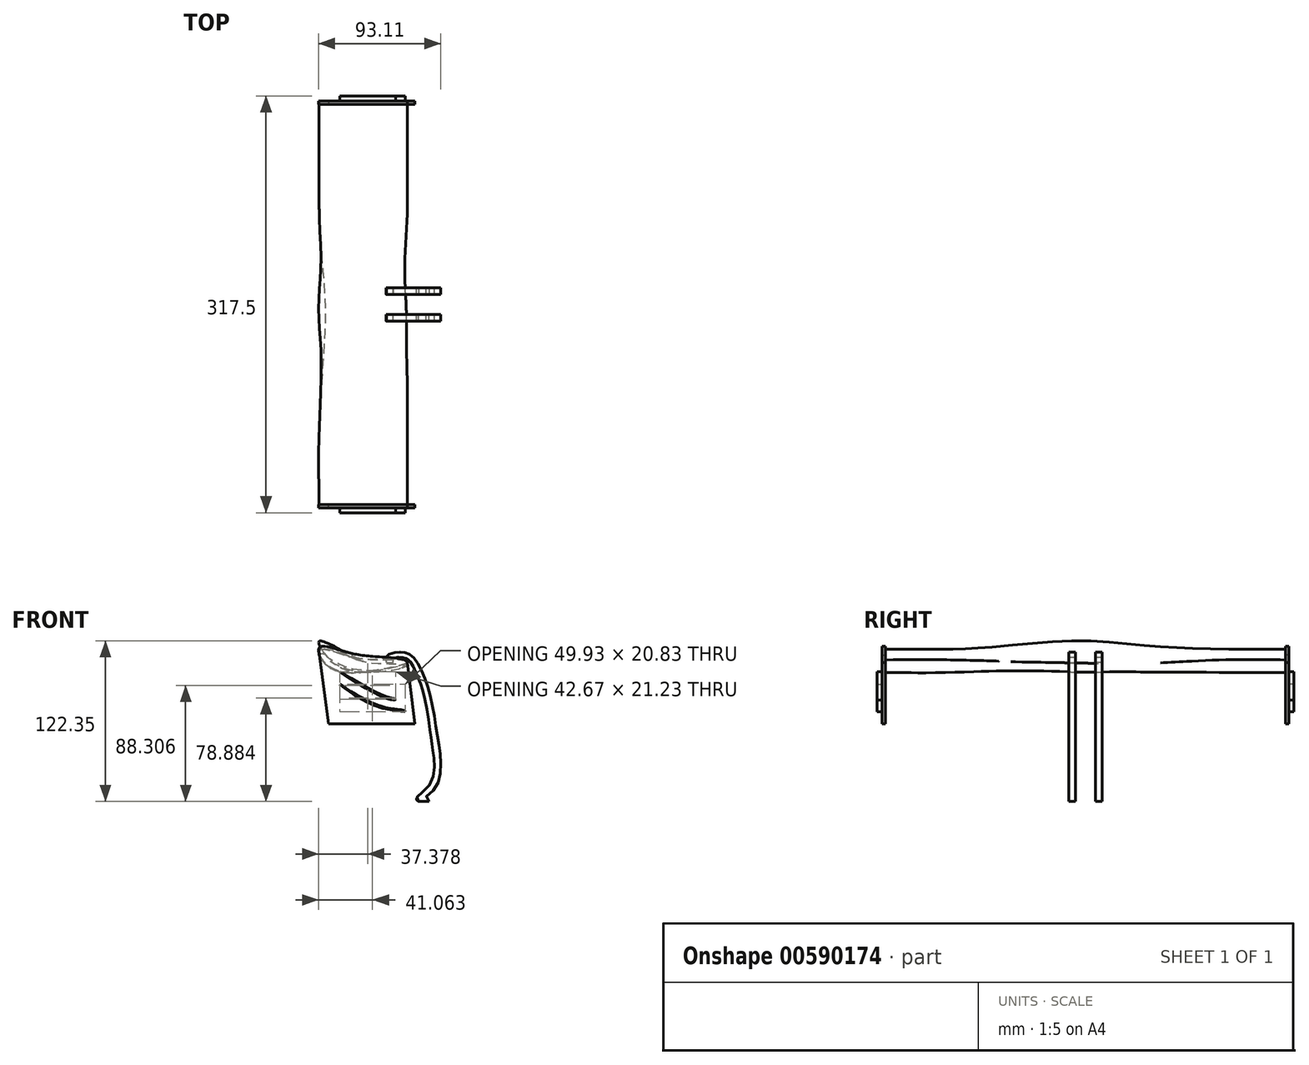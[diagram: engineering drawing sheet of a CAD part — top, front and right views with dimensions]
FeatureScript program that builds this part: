
annotation { "Feature Type Name" : "Feature", "Feature Type Description" : "" }
export const myFeature = defineFeature(function(context is Context, id is Id, definition is map)
    precondition{}
    {
        {
            var Q0;
            Q0=qCreatedBy(makeId("Front.planeOp"),FACE);
            cPlane(context, id + "F0", {"entities" : qUnion([Q0]), "cplaneType" : CPlaneType.OFFSET, "offset" : 50.8 * mm, "width" : 152.4 * mm, "height" : 152.4 * mm});
        }
        {
            var Q0;
            Q0=qCreatedBy(makeId("Front.planeOp"),FACE);
            cPlane(context, id + "F1", {"entities" : qUnion([Q0]), "cplaneType" : CPlaneType.OFFSET, "offset" : 101.6 * mm, "width" : 152.4 * mm, "height" : 152.4 * mm});
        }
        {
            var Q0;
            Q0=qCreatedBy(makeId("Front.planeOp"),FACE);
            cPlane(context, id + "F2", {"entities" : qUnion([Q0]), "cplaneType" : CPlaneType.OFFSET, "offset" : 152.4 * mm, "width" : 152.4 * mm, "height" : 152.4 * mm});
        }
        {
            var Q0;
            Q0=qCreatedBy(makeId("Front.planeOp"),FACE);
            cPlane(context, id + "F3", {"entities" : qUnion([Q0]), "cplaneType" : CPlaneType.OFFSET, "offset" : 203.2 * mm, "width" : 152.4 * mm, "height" : 152.4 * mm});
        }
        {
            var Q0;
            Q0=qCreatedBy(makeId("Front.planeOp"),FACE);
            var sketch = newSketch(context, id + "F4", { "sketchPlane" : qUnion([Q0])});
            skFitSpline(sketch, "E0", {"points": [v(-32.08, 8.38) * mm, v(-24.09, -3.15) * mm, v(7.76, -6.56) * mm, v(34.95, -0.3) * mm, v(34.95, 0.54) * mm, v(23.88, 1.97) * mm, v(-3.04, 3.1) * mm, v(-26.45, 10.12) * mm, v(-32.08, 8.38) * mm]});
            skSolve(sketch);
        }
        {
            var Q0;
            Q0=qCreatedBy(id+"F3.planeOp",FACE);
            var sketch = newSketch(context, id + "F5", { "sketchPlane" : qUnion([Q0])});
            skFitSpline(sketch, "E1", {"points": [v(-32.08, 8.38) * mm, v(-24.09, -3.15) * mm, v(7.76, -6.56) * mm, v(34.95, -0.3) * mm, v(34.95, 0.54) * mm, v(23.88, 1.97) * mm, v(-3.04, 3.1) * mm, v(-26.45, 10.12) * mm, v(-32.08, 8.38) * mm]});
            skSolve(sketch);
        }
        {
            var Q0;
            Q0=qCreatedBy(id+"F2.planeOp",FACE);
            var sketch = newSketch(context, id + "F6", { "sketchPlane" : qUnion([Q0])});
            skFitSpline(sketch, "E2", {"points": [v(-30.58, 9.5) * mm, v(-19.7, 0) * mm, v(6.57, -6.28) * mm, v(34.6, -1.74) * mm, v(34.6, -0.9) * mm, v(23.53, 0.54) * mm, v(-3.98, 3.65) * mm, v(-26.15, 13.6) * mm, v(-30.58, 9.5) * mm]});
            skSolve(sketch);
        }
        {
            var Q0;
            Q0=qCreatedBy(id+"F3.planeOp",FACE);
            cPlane(context, id + "F7", {"entities" : qUnion([Q0]), "cplaneType" : CPlaneType.OFFSET, "offset" : 50.8 * mm, "width" : 152.4 * mm, "height" : 152.4 * mm});
        }
        {
            var Q0;
            Q0=qCreatedBy(makeId("Front.planeOp"),FACE);
            cPlane(context, id + "F8", {"entities" : qUnion([Q0]), "cplaneType" : CPlaneType.OFFSET, "offset" : 50.8 * mm, "oppositeDirection" : true, "width" : 152.4 * mm, "height" : 152.4 * mm});
        }
        {
            var Q0;
            Q0=qCreatedBy(id+"F1.planeOp",FACE);
            var sketch = newSketch(context, id + "F9", { "sketchPlane" : qUnion([Q0])});
            skFitSpline(sketch, "E3", {"points": [v(-32.4, 15.38) * mm, v(-20.36, -1.02) * mm, v(5.9, -7.3) * mm, v(33.93, -2.76) * mm, v(33.93, -1.92) * mm, v(22.86, -0.49) * mm, v(-4.64, 2.63) * mm, v(-30.73, 16.4) * mm, v(-32.4, 15.38) * mm]});
            skSolve(sketch);
        }
        {
            var Q0;
            Q0=qCreatedBy(id+"F0.planeOp",FACE);
            var sketch = newSketch(context, id + "F10", { "sketchPlane" : qUnion([Q0])});
            skFitSpline(sketch, "E4", {"points": [v(-31.25, 8.48) * mm, v(-20.36, -1.02) * mm, v(5.9, -7.3) * mm, v(33.93, -2.76) * mm, v(33.93, -1.92) * mm, v(22.86, -0.49) * mm, v(-4.64, 2.63) * mm, v(-26.82, 12.57) * mm, v(-31.25, 8.48) * mm]});
            skSolve(sketch);
        }
        {
            var Q0;
            Q0=qCreatedBy(id+"F7.planeOp",FACE);
            var sketch = newSketch(context, id + "F11", { "sketchPlane" : qUnion([Q0])});
            skFitSpline(sketch, "E5", {"points": [v(-32.08, 8.38) * mm, v(-24.09, -3.15) * mm, v(7.76, -6.56) * mm, v(34.95, -0.3) * mm, v(34.95, 0.54) * mm, v(23.88, 1.97) * mm, v(-3.04, 3.1) * mm, v(-26.45, 10.12) * mm, v(-32.08, 8.38) * mm]});
            skSolve(sketch);
        }
        {
            var Q0;
            Q0=qCreatedBy(id+"F8.planeOp",FACE);
            var sketch = newSketch(context, id + "F12", { "sketchPlane" : qUnion([Q0])});
            skFitSpline(sketch, "E6", {"points": [v(-32.08, 8.38) * mm, v(-24.09, -3.15) * mm, v(7.76, -6.56) * mm, v(34.95, -0.3) * mm, v(34.95, 0.54) * mm, v(23.88, 1.97) * mm, v(-3.04, 3.1) * mm, v(-26.45, 10.12) * mm, v(-32.08, 8.38) * mm]});
            skSolve(sketch);
        }
        {
            var Q0;
            Q0=makeQuery(id+"F11.imprint","IMPRINT",FACE,{"disambiguationData":[TD([[makeQuery(id+"F11.imprint","IMPRINT",EDGE,{"derivedFrom":sQuery(id+"F11.wireOp",EDGE,"E5")}),1.0]])]});
            var Q1;
            Q1=makeQuery(id+"F5.imprint","IMPRINT",FACE,{"disambiguationData":[TD([[makeQuery(id+"F5.imprint","IMPRINT",EDGE,{"derivedFrom":sQuery(id+"F5.wireOp",EDGE,"E1")}),1.0]])]});
            var Q2;
            Q2=makeQuery(id+"F6.imprint","IMPRINT",FACE,{"disambiguationData":[TD([[makeQuery(id+"F6.imprint","IMPRINT",EDGE,{"derivedFrom":sQuery(id+"F6.wireOp",EDGE,"E2")}),1.0]])]});
            var Q3;
            Q3=makeQuery(id+"F9.imprint","IMPRINT",FACE,{"disambiguationData":[TD([[makeQuery(id+"F9.imprint","IMPRINT",EDGE,{"derivedFrom":sQuery(id+"F9.wireOp",EDGE,"E3")}),1.0]])]});
            var Q4;
            Q4=makeQuery(id+"F10.imprint","IMPRINT",FACE,{"disambiguationData":[TD([[makeQuery(id+"F10.imprint","IMPRINT",EDGE,{"derivedFrom":sQuery(id+"F10.wireOp",EDGE,"E4")}),1.0]])]});
            var Q5;
            Q5=makeQuery(id+"F4.imprint","IMPRINT",FACE,{"disambiguationData":[TD([[makeQuery(id+"F4.imprint","IMPRINT",EDGE,{"derivedFrom":sQuery(id+"F4.wireOp",EDGE,"E0")}),1.0]])]});
            var Q6;
            Q6=makeQuery(id+"F12.imprint","IMPRINT",FACE,{"disambiguationData":[TD([[makeQuery(id+"F12.imprint","IMPRINT",EDGE,{"derivedFrom":sQuery(id+"F12.wireOp",EDGE,"E6")}),1.0]])]});
            loft(context, id + "F13", {"sheetProfilesArray" : [{ "sheetProfileEntities" : qUnion([Q0]) }, { "sheetProfileEntities" : qUnion([Q1]) }, { "sheetProfileEntities" : qUnion([Q2]) }, { "sheetProfileEntities" : qUnion([Q3]) }, { "sheetProfileEntities" : qUnion([Q4]) }, { "sheetProfileEntities" : qUnion([Q5]) }, { "sheetProfileEntities" : qUnion([Q6]) }]});
        }
        {
            var Q0;
            Q0=qCreatedBy(id+"F8.planeOp",FACE);
            var sketch = newSketch(context, id + "F14", { "sketchPlane" : qUnion([Q0])});
            skLineSegment(sketch, "E7", {"start": v(40.97, -46.8) * mm, "end": v(-24.74, -46.8) * mm});
            skFitSpline(sketch, "E8", {"points": [v(35.16, 0) * mm, v(1.01, 5.43) * mm, v(-26.43, 12.16) * mm, v(-31.74, 5.63) * mm], "startDerivative": vector(5.48, 30.94) * mm, "endDerivative": vector(34.9, -100.77) * mm});
            skLineSegment(sketch, "E9", {"start": v(35.16, 0) * mm, "end": v(40.97, -46.8) * mm});
            skLineSegment(sketch, "E10", {"start": v(20.11, -39.48) * mm, "end": v(16.28, -8.63) * mm});
            skLineSegment(sketch, "E11", {"start": v(16.28, -8.63) * mm, "end": v(14.52, -8.63) * mm});
            skLineSegment(sketch, "E12", {"start": v(20.11, -39.48) * mm, "end": v(18.36, -39.48) * mm});
            skLineSegment(sketch, "E13", {"start": v(18.36, -39.48) * mm, "end": v(14.52, -8.63) * mm});
            skLineSegment(sketch, "E14", {"start": v(-31.74, 5.63) * mm, "end": v(-24.74, -46.8) * mm});
            skSolve(sketch);
        }
        {
            var Q0;
            Q0=sQuery(id+"F14.wireOp",EDGE,"E7");
            var Q1;
            Q1=sQuery(id+"F14.wireOp",EDGE,"E8");
            loft(context, id + "F15", {"bodyType" : ToolBodyType.SURFACE, "wireProfilesArray" : [{ "wireProfileEntities" : qUnion([Q0]) }, { "wireProfileEntities" : qUnion([Q1]) }]});
        }
        {
            var Q0;
            Q0=makeQuery(id+"F15.opLoft","SWEPT_FACE",FACE,{"disambiguationData":[OSD([sQuery(id+"F14.wireOp",VERTEX,"E7.start"),sQuery(id+"F14.wireOp",VERTEX,"E7.end"),sQuery(id+"F14.wireOp",VERTEX,"E8.start"),sQuery(id+"F14.wireOp",VERTEX,"E8.end"),sQuery(id+"F14.wireOp",EDGE,"E7"),sQuery(id+"F14.wireOp",EDGE,"E8")])]});
            extrude(context, id + "F16", {"entities" : qUnion([Q0]), "operationType" : NewBodyOperationType.ADD, "depth" : 2.54 * mm, "offsetDistance" : 25.4 * mm});
        }
        {
            var Q0;
            Q0=makeQuery(id+"F16.opExtrude","CAP_FACE",FACE,{"disambiguationData":[OSD([sQuery(id+"F14.wireOp",VERTEX,"E7.start"),sQuery(id+"F14.wireOp",VERTEX,"E7.end"),sQuery(id+"F14.wireOp",VERTEX,"E8.start"),sQuery(id+"F14.wireOp",VERTEX,"E8.end"),sQuery(id+"F14.wireOp",EDGE,"E7"),sQuery(id+"F14.wireOp",EDGE,"E8")])],"isStart":false});
            extrude(context, id + "F17", {"entities" : qUnion([Q0]), "operationType" : NewBodyOperationType.ADD, "oppositeDirection" : true, "depth" : 309.88 * mm, "offsetDistance" : 25.4 * mm, "hasSecondDirection" : true, "secondDirectionOppositeDirection" : true, "secondDirectionDepth" : 307.34 * mm});
        }
        {
            var Q0;
            Q0=qCreatedBy(id+"F1.planeOp",FACE);
            var sketch = newSketch(context, id + "F18", { "sketchPlane" : qUnion([Q0])});
            skFitSpline(sketch, "E15", {"points": [v(19.23, 0) * mm, v(19.53, 5.21) * mm, v(26.93, 7.66) * mm, v(32.91, 7.66) * mm, v(39.21, 4.45) * mm, v(46.2, -6.87) * mm, v(53.05, -27.43) * mm, v(57.63, -53.41) * mm, v(60.54, -75.73) * mm, v(54.74, -97.36) * mm, v(51.6, -105.82) * mm], "startDerivative": vector(-10.79, 100.54) * mm, "endDerivative": vector(210.36, -102.87) * mm});
            skFitSpline(sketch, "E16", {"points": [v(24.3, 0) * mm, v(25.55, 3.58) * mm, v(31.17, 3.78) * mm, v(36.62, 1.47) * mm, v(42.2, -8.88) * mm, v(47.35, -22.74) * mm, v(52.78, -54.1) * mm, v(54.9, -69.29) * mm, v(50.8, -94.97) * mm, v(43.76, -105.82) * mm], "startDerivative": vector(-14.55, 95.95) * mm, "endDerivative": vector(143.72, -76.8) * mm});
            skSolve(sketch);
        }
        {
            var Q0;
            Q0=sQuery(id+"F18.wireOp",EDGE,"E15");
            var Q1;
            Q1=sQuery(id+"F18.wireOp",EDGE,"E16");
            loft(context, id + "F19", {"bodyType" : ToolBodyType.SURFACE, "wireProfilesArray" : [{ "wireProfileEntities" : qUnion([Q0]) }, { "wireProfileEntities" : qUnion([Q1]) }]});
        }
        {
            var Q0;
            Q0=makeQuery(id+"F19.opLoft","SWEPT_FACE",FACE,{"disambiguationData":[OSD([sQuery(id+"F18.wireOp",VERTEX,"E15.start"),sQuery(id+"F18.wireOp",VERTEX,"E15.end"),sQuery(id+"F18.wireOp",VERTEX,"E16.start"),sQuery(id+"F18.wireOp",VERTEX,"E16.end"),sQuery(id+"F18.wireOp",EDGE,"E15"),sQuery(id+"F18.wireOp",EDGE,"E16")])]});
            extrude(context, id + "F20", {"entities" : qUnion([Q0]), "depth" : 12.7 * mm, "offsetDistance" : 25.4 * mm, "hasSecondDirection" : true, "secondDirectionOppositeDirection" : false, "secondDirectionDepth" : 7.62 * mm});
        }
        {
            var Q0;
            Q0=makeQuery(id+"F19.opLoft","SWEPT_FACE",FACE,{"disambiguationData":[OSD([sQuery(id+"F18.wireOp",VERTEX,"E15.start"),sQuery(id+"F18.wireOp",VERTEX,"E15.end"),sQuery(id+"F18.wireOp",VERTEX,"E16.start"),sQuery(id+"F18.wireOp",VERTEX,"E16.end"),sQuery(id+"F18.wireOp",EDGE,"E15"),sQuery(id+"F18.wireOp",EDGE,"E16")])]});
            extrude(context, id + "F21", {"entities" : qUnion([Q0]), "oppositeDirection" : true, "depth" : 12.7 * mm, "offsetDistance" : 25.4 * mm, "hasSecondDirection" : true, "secondDirectionOppositeDirection" : true, "secondDirectionDepth" : 7.62 * mm});
        }
        {
            var Q0;
            Q0=qCreatedBy(id+"F7.planeOp",FACE);
            var sketch = newSketch(context, id + "F22", { "sketchPlane" : qUnion([Q0])});
            skFitSpline(sketch, "E17", {"points": [v(-16.4, -16.52) * mm, v(25.61, -36.45) * mm, v(33.54, -37.35) * mm], "startDerivative": vector(93.67, -75.9) * mm, "endDerivative": vector(22.32, 0.58) * mm});
            skFitSpline(sketch, "E18", {"points": [v(-16.4, -16.52) * mm, v(25.84, -35.43) * mm, v(33.54, -37.35) * mm], "startDerivative": vector(105.67, -69.65) * mm, "endDerivative": vector(0, -9.28) * mm});
            skSolve(sketch);
        }
        {
            var Q0;
            Q0 = qSketchRegion(id + "F22", true);
            extrude(context, id + "F23", {"entities" : qUnion([Q0]), "operationType" : NewBodyOperationType.ADD, "depth" : 6.35 * mm, "offsetDistance" : 25.4 * mm});
        }
        {
            var Q0;
            Q0=qCreatedBy(id+"F7.planeOp",FACE);
            var sketch = newSketch(context, id + "F24", { "sketchPlane" : qUnion([Q0])});
            skFitSpline(sketch, "E19", {"points": [v(-16.45, -6.9) * mm, v(16.75, -24.98) * mm, v(26.13, -27.84) * mm, v(26.13, -28.35) * mm, v(15.8, -25.97) * mm, v(-16.45, -6.9) * mm]});
            skSolve(sketch);
        }
        {
            var Q0;
            Q0 = qSketchRegion(id + "F24", true);
            extrude(context, id + "F25", {"entities" : qUnion([Q0]), "operationType" : NewBodyOperationType.ADD, "depth" : 6.35 * mm, "offsetDistance" : 25.4 * mm});
        }
        {
            var Q0;
            Q0=makeQuery(id+"F25.opExtrude","CAP_FACE",FACE,{"disambiguationData":[OSD([sQuery(id+"F24.wireOp",EDGE,"E19")])],"isStart":false});
            var Q1;
            Q1=makeQuery(id+"F23.opExtrude","CAP_FACE",FACE,{"disambiguationData":[OSD([sQuery(id+"F22.wireOp",EDGE,"E17"),sQuery(id+"F22.wireOp",EDGE,"E18")])],"isStart":false});
            extrude(context, id + "F26", {"entities" : qUnion([Q0, Q1]), "operationType" : NewBodyOperationType.ADD, "oppositeDirection" : true, "depth" : 317.5 * mm, "offsetDistance" : 25.4 * mm, "hasSecondDirection" : true, "secondDirectionOppositeDirection" : true, "secondDirectionDepth" : 311.15 * mm});
        }
    });
